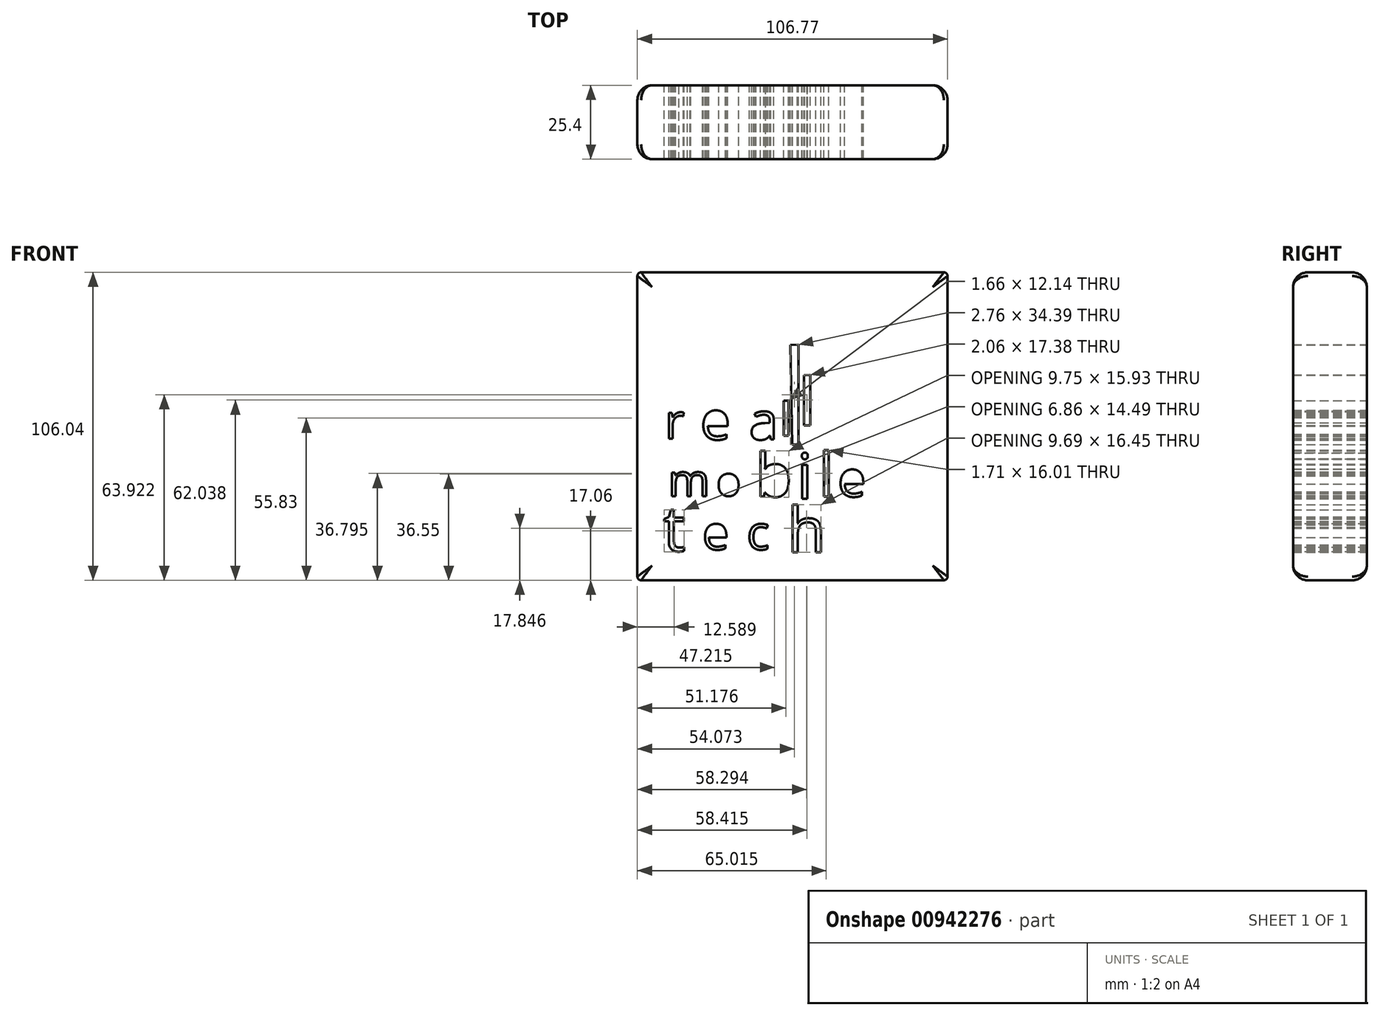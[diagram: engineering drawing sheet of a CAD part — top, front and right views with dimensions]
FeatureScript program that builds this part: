
annotation { "Feature Type Name" : "Feature", "Feature Type Description" : "" }
export const myFeature = defineFeature(function(context is Context, id is Id, definition is map)
    precondition{}
    {
        {
            var Q0;
            Q0=qCreatedBy(makeId("Front.planeOp"),FACE);
            var sketch = newSketch(context, id + "F0", { "sketchPlane" : qUnion([Q0])});
            skText(sketch, "E0", { "text": "r", "fontName": "OpenSans-Regular.ttf"});
            skText(sketch, "E1", { "text": "e", "fontName": "OpenSans-Regular.ttf"});
            skText(sketch, "E2", { "text": "a\n", "fontName": "OpenSans-Regular.ttf"});
            skLineSegment(sketch, "E3", {"start": v(-13.31, 13.45) * mm, "end": v(-13.31, 1.31) * mm});
            skLineSegment(sketch, "E4", {"start": v(-13.31, 1.31) * mm, "end": v(-11.66, 1.31) * mm});
            skLineSegment(sketch, "E5", {"start": v(-11.66, 1.31) * mm, "end": v(-11.66, 13.45) * mm});
            skLineSegment(sketch, "E6", {"start": v(-11.66, 13.45) * mm, "end": v(-13.31, 13.45) * mm});
            skLineSegment(sketch, "E7", {"start": v(-10.42, -1.72) * mm, "end": v(-8.2, -1.72) * mm});
            skLineSegment(sketch, "E8", {"start": v(-10.97, 32.62) * mm, "end": v(-10.42, -1.72) * mm});
            skLineSegment(sketch, "E9", {"start": v(-10.97, 32.62) * mm, "end": v(-8.2, 32.67) * mm});
            skLineSegment(sketch, "E10", {"start": v(-8.2, 32.67) * mm, "end": v(-8.2, -1.72) * mm});
            skLineSegment(sketch, "E11", {"start": v(-6.28, 22.14) * mm, "end": v(-6.28, 4.9) * mm});
            skLineSegment(sketch, "E12", {"start": v(-6.28, 4.9) * mm, "end": v(-4.21, 4.93) * mm});
            skLineSegment(sketch, "E13", {"start": v(-4.21, 4.93) * mm, "end": v(-4.21, 22.28) * mm});
            skLineSegment(sketch, "E14", {"start": v(-4.21, 22.28) * mm, "end": v(-6.28, 22.14) * mm});
            skText(sketch, "E15", { "text": "m", "fontName": "OpenSans-Regular.ttf"});
            skText(sketch, "E16", { "text": "o", "fontName": "OpenSans-Regular.ttf"});
            skText(sketch, "E17", { "text": "b", "fontName": "OpenSans-Regular.ttf"});
            skText(sketch, "E18", { "text": "i", "fontName": "OpenSans-Regular.ttf"});
            skText(sketch, "E19", { "text": "l", "fontName": "OpenSans-Regular.ttf"});
            skText(sketch, "E20", { "text": "e", "fontName": "OpenSans-Regular.ttf"});
            skText(sketch, "E21", { "text": "t\n", "fontName": "OpenSans-Regular.ttf"});
            skText(sketch, "E22", { "text": "e", "fontName": "OpenSans-Regular.ttf"});
            skText(sketch, "E23", { "text": "c", "fontName": "OpenSans-Regular.ttf"});
            skText(sketch, "E24", { "text": "h", "fontName": "OpenSans-Regular.ttf"});
            skLineSegment(sketch, "E25", {"start": v(-63.66, 57.6) * mm, "end": v(-63.66, -50.42) * mm});
            skLineSegment(sketch, "E26", {"start": v(-63.66, -48.45) * mm, "end": v(43.1, -48.45) * mm});
            skLineSegment(sketch, "E27", {"start": v(43.1, 57.6) * mm, "end": v(43.1, -48.45) * mm});
            skLineSegment(sketch, "E28", {"start": v(-63.66, 57.6) * mm, "end": v(43.1, 57.6) * mm});
            const initialGuessF0  = {"E0": [-0.05428, 0.00034, 1, 0, 0.012], "E1": [-0.042, 0, 1, 0, 0.01331], "E2": [-0.02518, 0, 1, 0, 0.0129], "E15": [-0.05304, -0.01952, 1, 0, 0.01104], "E16": [-0.03649, -0.01938, 1, 0, 0.01007], "E17": [-0.0231, -0.01966, 1, 0, 0.0149], "E18": [-0.00876, -0.02035, 1, 0, 0.01559], "E19": [-0.00131, -0.01966, 1, 0, 0.01517], "E20": [0.00531, -0.01966, 1, 0, 0.01242], "E21": [-0.05483, -0.03842, 1, 0, 0.01559], "E22": [-0.04132, -0.03787, 1, 0, 0.01173], "E23": [-0.026, -0.03787, 1, 0, 0.01173], "E24": [-0.01207, -0.03883, 1, 0, 0.01559]};
            skSetInitialGuess(sketch, initialGuessF0);
            skSolve(sketch);
        }
        {
            var Q0;
            Q0 = qSketchRegion(id + "F0", true);
            extrude(context, id + "F1", {"entities" : qUnion([Q0]), "depth" : 25.4 * mm, "offsetDistance" : 25.4 * mm});
        }
        {
            var Q0;
            Q0=makeQuery(id+"F1.opExtrude","SWEPT_EDGE",EDGE,{"disambiguationData":[OSD([sQuery(id+"F0.wireOp",EDGE,"E27"),sQuery(id+"F0.wireOp",EDGE,"E28")])]});
            var Q1;
            Q1=makeQuery(id+"F1.opExtrude","SWEPT_EDGE",EDGE,{"disambiguationData":[OSD([sQuery(id+"F0.wireOp",EDGE,"E26"),sQuery(id+"F0.wireOp",EDGE,"E27")])]});
            var Q2;
            Q2=makeQuery(id+"F1.opExtrude","SWEPT_EDGE",EDGE,{"disambiguationData":[OSD([sQuery(id+"F0.wireOp",EDGE,"E25"),sQuery(id+"F0.wireOp",EDGE,"E26")])]});
            var Q3;
            Q3=makeQuery(id+"F1.opExtrude","SWEPT_EDGE",EDGE,{"disambiguationData":[OSD([sQuery(id+"F0.wireOp",EDGE,"E25"),sQuery(id+"F0.wireOp",EDGE,"E28")])]});
            fillet(context, id + "F2", {"entities" : qUnion([Q0, Q1, Q2, Q3]), "radius" : 1.27 * mm, "tangentPropagation" : true, "allowEdgeOverflow" : false});
        }
        {
            var Q0;
            Q0=makeQuery(id+"F1.opExtrude","CAP_EDGE",EDGE,{"disambiguationData":[OSD([sQuery(id+"F0.wireOp",EDGE,"E28")])],"isStart":false});
            var Q1;
            {var subQ0=sQuery(id+"F0.wireOp",EDGE,"E28");var subQ1=sQuery(id+"F0.wireOp",EDGE,"E27");Q1=makeQuery(id+"F2.opFillet","BLEND_EDGE",EDGE,{"blendedFrom":[makeQuery(id+"F1.opExtrude","SWEPT_EDGE",EDGE,{"disambiguationData":[OSD([subQ1,subQ0])]}),makeQuery(id+"F1.opExtrude","CAP_FACE",FACE,{"disambiguationData":[OSD([sQuery(id+"F0.wireOp",EDGE,"E0.sketch_text.stroke-0"),sQuery(id+"F0.wireOp",EDGE,"E0.sketch_text.stroke-1"),sQuery(id+"F0.wireOp",EDGE,"E0.sketch_text.stroke-2"),sQuery(id+"F0.wireOp",EDGE,"E0.sketch_text.stroke-3"),sQuery(id+"F0.wireOp",EDGE,"E0.sketch_text.stroke-4"),sQuery(id+"F0.wireOp",EDGE,"E0.sketch_text.stroke-5"),sQuery(id+"F0.wireOp",EDGE,"E0.sketch_text.stroke-6"),sQuery(id+"F0.wireOp",EDGE,"E0.sketch_text.stroke-7"),sQuery(id+"F0.wireOp",EDGE,"E0.sketch_text.stroke-8"),sQuery(id+"F0.wireOp",EDGE,"E0.sketch_text.stroke-9"),sQuery(id+"F0.wireOp",EDGE,"E0.sketch_text.stroke-10"),sQuery(id+"F0.wireOp",EDGE,"E0.sketch_text.stroke-11"),sQuery(id+"F0.wireOp",EDGE,"E0.sketch_text.stroke-12"),sQuery(id+"F0.wireOp",EDGE,"E1.sketch_text.stroke-0"),sQuery(id+"F0.wireOp",EDGE,"E1.sketch_text.stroke-1"),sQuery(id+"F0.wireOp",EDGE,"E1.sketch_text.stroke-2"),sQuery(id+"F0.wireOp",EDGE,"E1.sketch_text.stroke-3"),sQuery(id+"F0.wireOp",EDGE,"E1.sketch_text.stroke-4"),sQuery(id+"F0.wireOp",EDGE,"E1.sketch_text.stroke-5"),sQuery(id+"F0.wireOp",EDGE,"E1.sketch_text.stroke-6"),sQuery(id+"F0.wireOp",EDGE,"E1.sketch_text.stroke-7"),sQuery(id+"F0.wireOp",EDGE,"E1.sketch_text.stroke-8"),sQuery(id+"F0.wireOp",EDGE,"E1.sketch_text.stroke-9"),sQuery(id+"F0.wireOp",EDGE,"E1.sketch_text.stroke-10"),sQuery(id+"F0.wireOp",EDGE,"E1.sketch_text.stroke-11"),sQuery(id+"F0.wireOp",EDGE,"E1.sketch_text.stroke-12"),sQuery(id+"F0.wireOp",EDGE,"E1.sketch_text.stroke-13"),sQuery(id+"F0.wireOp",EDGE,"E2.sketch_text.stroke-0"),sQuery(id+"F0.wireOp",EDGE,"E2.sketch_text.stroke-1"),sQuery(id+"F0.wireOp",EDGE,"E2.sketch_text.stroke-2"),sQuery(id+"F0.wireOp",EDGE,"E2.sketch_text.stroke-3"),sQuery(id+"F0.wireOp",EDGE,"E2.sketch_text.stroke-4"),sQuery(id+"F0.wireOp",EDGE,"E2.sketch_text.stroke-5"),sQuery(id+"F0.wireOp",EDGE,"E2.sketch_text.stroke-6"),sQuery(id+"F0.wireOp",EDGE,"E2.sketch_text.stroke-7"),sQuery(id+"F0.wireOp",EDGE,"E2.sketch_text.stroke-8"),sQuery(id+"F0.wireOp",EDGE,"E2.sketch_text.stroke-9"),sQuery(id+"F0.wireOp",EDGE,"E2.sketch_text.stroke-10"),sQuery(id+"F0.wireOp",EDGE,"E2.sketch_text.stroke-11"),sQuery(id+"F0.wireOp",EDGE,"E2.sketch_text.stroke-12"),sQuery(id+"F0.wireOp",EDGE,"E2.sketch_text.stroke-13"),sQuery(id+"F0.wireOp",EDGE,"E2.sketch_text.stroke-14"),sQuery(id+"F0.wireOp",EDGE,"E2.sketch_text.stroke-15"),sQuery(id+"F0.wireOp",EDGE,"E2.sketch_text.stroke-16"),sQuery(id+"F0.wireOp",EDGE,"E2.sketch_text.stroke-17"),sQuery(id+"F0.wireOp",EDGE,"E2.sketch_text.stroke-18"),sQuery(id+"F0.wireOp",EDGE,"E3"),sQuery(id+"F0.wireOp",EDGE,"E4"),sQuery(id+"F0.wireOp",EDGE,"E5"),sQuery(id+"F0.wireOp",EDGE,"E6"),sQuery(id+"F0.wireOp",EDGE,"E7"),sQuery(id+"F0.wireOp",EDGE,"E8"),sQuery(id+"F0.wireOp",EDGE,"E9"),sQuery(id+"F0.wireOp",EDGE,"E10"),sQuery(id+"F0.wireOp",EDGE,"E11"),sQuery(id+"F0.wireOp",EDGE,"E12"),sQuery(id+"F0.wireOp",EDGE,"E13"),sQuery(id+"F0.wireOp",EDGE,"E14"),sQuery(id+"F0.wireOp",EDGE,"E15.sketch_text.stroke-0"),sQuery(id+"F0.wireOp",EDGE,"E15.sketch_text.stroke-1"),sQuery(id+"F0.wireOp",EDGE,"E15.sketch_text.stroke-2"),sQuery(id+"F0.wireOp",EDGE,"E15.sketch_text.stroke-3"),sQuery(id+"F0.wireOp",EDGE,"E15.sketch_text.stroke-4"),sQuery(id+"F0.wireOp",EDGE,"E15.sketch_text.stroke-5"),sQuery(id+"F0.wireOp",EDGE,"E15.sketch_text.stroke-6"),sQuery(id+"F0.wireOp",EDGE,"E15.sketch_text.stroke-7"),sQuery(id+"F0.wireOp",EDGE,"E15.sketch_text.stroke-8"),sQuery(id+"F0.wireOp",EDGE,"E15.sketch_text.stroke-9"),sQuery(id+"F0.wireOp",EDGE,"E15.sketch_text.stroke-10"),sQuery(id+"F0.wireOp",EDGE,"E15.sketch_text.stroke-11"),sQuery(id+"F0.wireOp",EDGE,"E15.sketch_text.stroke-12"),sQuery(id+"F0.wireOp",EDGE,"E15.sketch_text.stroke-13"),sQuery(id+"F0.wireOp",EDGE,"E15.sketch_text.stroke-14"),sQuery(id+"F0.wireOp",EDGE,"E15.sketch_text.stroke-15"),sQuery(id+"F0.wireOp",EDGE,"E15.sketch_text.stroke-16"),sQuery(id+"F0.wireOp",EDGE,"E15.sketch_text.stroke-17"),sQuery(id+"F0.wireOp",EDGE,"E15.sketch_text.stroke-18"),sQuery(id+"F0.wireOp",EDGE,"E15.sketch_text.stroke-19"),sQuery(id+"F0.wireOp",EDGE,"E15.sketch_text.stroke-20"),sQuery(id+"F0.wireOp",EDGE,"E15.sketch_text.stroke-21"),sQuery(id+"F0.wireOp",EDGE,"E15.sketch_text.stroke-22"),sQuery(id+"F0.wireOp",EDGE,"E15.sketch_text.stroke-23"),sQuery(id+"F0.wireOp",EDGE,"E15.sketch_text.stroke-24"),sQuery(id+"F0.wireOp",EDGE,"E15.sketch_text.stroke-25"),sQuery(id+"F0.wireOp",EDGE,"E15.sketch_text.stroke-26"),sQuery(id+"F0.wireOp",EDGE,"E15.sketch_text.stroke-27"),sQuery(id+"F0.wireOp",EDGE,"E16.sketch_text.stroke-0"),sQuery(id+"F0.wireOp",EDGE,"E16.sketch_text.stroke-1"),sQuery(id+"F0.wireOp",EDGE,"E16.sketch_text.stroke-2"),sQuery(id+"F0.wireOp",EDGE,"E16.sketch_text.stroke-3"),sQuery(id+"F0.wireOp",EDGE,"E16.sketch_text.stroke-4"),sQuery(id+"F0.wireOp",EDGE,"E16.sketch_text.stroke-5"),sQuery(id+"F0.wireOp",EDGE,"E16.sketch_text.stroke-6"),sQuery(id+"F0.wireOp",EDGE,"E16.sketch_text.stroke-7"),sQuery(id+"F0.wireOp",EDGE,"E16.sketch_text.stroke-8"),sQuery(id+"F0.wireOp",EDGE,"E17.sketch_text.stroke-0"),sQuery(id+"F0.wireOp",EDGE,"E17.sketch_text.stroke-1"),sQuery(id+"F0.wireOp",EDGE,"E17.sketch_text.stroke-2"),sQuery(id+"F0.wireOp",EDGE,"E17.sketch_text.stroke-3"),sQuery(id+"F0.wireOp",EDGE,"E17.sketch_text.stroke-4"),sQuery(id+"F0.wireOp",EDGE,"E17.sketch_text.stroke-5"),sQuery(id+"F0.wireOp",EDGE,"E17.sketch_text.stroke-6"),sQuery(id+"F0.wireOp",EDGE,"E17.sketch_text.stroke-7"),sQuery(id+"F0.wireOp",EDGE,"E17.sketch_text.stroke-8"),sQuery(id+"F0.wireOp",EDGE,"E17.sketch_text.stroke-9"),sQuery(id+"F0.wireOp",EDGE,"E17.sketch_text.stroke-10"),sQuery(id+"F0.wireOp",EDGE,"E17.sketch_text.stroke-11"),sQuery(id+"F0.wireOp",EDGE,"E17.sketch_text.stroke-12"),sQuery(id+"F0.wireOp",EDGE,"E17.sketch_text.stroke-13"),sQuery(id+"F0.wireOp",EDGE,"E17.sketch_text.stroke-14"),sQuery(id+"F0.wireOp",EDGE,"E18.sketch_text.stroke-0"),sQuery(id+"F0.wireOp",EDGE,"E18.sketch_text.stroke-1"),sQuery(id+"F0.wireOp",EDGE,"E18.sketch_text.stroke-2"),sQuery(id+"F0.wireOp",EDGE,"E18.sketch_text.stroke-3"),sQuery(id+"F0.wireOp",EDGE,"E18.sketch_text.stroke-4"),sQuery(id+"F0.wireOp",EDGE,"E18.sketch_text.stroke-5"),sQuery(id+"F0.wireOp",EDGE,"E18.sketch_text.stroke-6"),sQuery(id+"F0.wireOp",EDGE,"E18.sketch_text.stroke-7"),sQuery(id+"F0.wireOp",EDGE,"E18.sketch_text.stroke-8"),sQuery(id+"F0.wireOp",EDGE,"E18.sketch_text.stroke-9"),sQuery(id+"F0.wireOp",EDGE,"E18.sketch_text.stroke-10"),sQuery(id+"F0.wireOp",EDGE,"E18.sketch_text.stroke-11"),sQuery(id+"F0.wireOp",EDGE,"E19.sketch_text.stroke-0"),sQuery(id+"F0.wireOp",EDGE,"E19.sketch_text.stroke-1"),sQuery(id+"F0.wireOp",EDGE,"E19.sketch_text.stroke-2"),sQuery(id+"F0.wireOp",EDGE,"E19.sketch_text.stroke-3"),sQuery(id+"F0.wireOp",EDGE,"E20.sketch_text.stroke-0"),sQuery(id+"F0.wireOp",EDGE,"E20.sketch_text.stroke-1"),sQuery(id+"F0.wireOp",EDGE,"E20.sketch_text.stroke-2"),sQuery(id+"F0.wireOp",EDGE,"E20.sketch_text.stroke-3"),sQuery(id+"F0.wireOp",EDGE,"E20.sketch_text.stroke-4"),sQuery(id+"F0.wireOp",EDGE,"E20.sketch_text.stroke-5"),sQuery(id+"F0.wireOp",EDGE,"E20.sketch_text.stroke-6"),sQuery(id+"F0.wireOp",EDGE,"E20.sketch_text.stroke-7"),sQuery(id+"F0.wireOp",EDGE,"E20.sketch_text.stroke-8"),sQuery(id+"F0.wireOp",EDGE,"E20.sketch_text.stroke-9"),sQuery(id+"F0.wireOp",EDGE,"E20.sketch_text.stroke-10"),sQuery(id+"F0.wireOp",EDGE,"E20.sketch_text.stroke-11"),sQuery(id+"F0.wireOp",EDGE,"E20.sketch_text.stroke-12"),sQuery(id+"F0.wireOp",EDGE,"E20.sketch_text.stroke-13"),sQuery(id+"F0.wireOp",EDGE,"E21.sketch_text.stroke-0"),sQuery(id+"F0.wireOp",EDGE,"E21.sketch_text.stroke-1"),sQuery(id+"F0.wireOp",EDGE,"E21.sketch_text.stroke-2"),sQuery(id+"F0.wireOp",EDGE,"E21.sketch_text.stroke-3"),sQuery(id+"F0.wireOp",EDGE,"E21.sketch_text.stroke-4"),sQuery(id+"F0.wireOp",EDGE,"E21.sketch_text.stroke-5"),sQuery(id+"F0.wireOp",EDGE,"E21.sketch_text.stroke-6"),sQuery(id+"F0.wireOp",EDGE,"E21.sketch_text.stroke-7"),sQuery(id+"F0.wireOp",EDGE,"E21.sketch_text.stroke-8"),sQuery(id+"F0.wireOp",EDGE,"E21.sketch_text.stroke-9"),sQuery(id+"F0.wireOp",EDGE,"E21.sketch_text.stroke-10"),sQuery(id+"F0.wireOp",EDGE,"E21.sketch_text.stroke-11"),sQuery(id+"F0.wireOp",EDGE,"E21.sketch_text.stroke-12"),sQuery(id+"F0.wireOp",EDGE,"E21.sketch_text.stroke-13"),sQuery(id+"F0.wireOp",EDGE,"E21.sketch_text.stroke-14"),sQuery(id+"F0.wireOp",EDGE,"E21.sketch_text.stroke-15"),sQuery(id+"F0.wireOp",EDGE,"E21.sketch_text.stroke-16"),sQuery(id+"F0.wireOp",EDGE,"E21.sketch_text.stroke-17"),sQuery(id+"F0.wireOp",EDGE,"E21.sketch_text.stroke-18"),sQuery(id+"F0.wireOp",EDGE,"E22.sketch_text.stroke-0"),sQuery(id+"F0.wireOp",EDGE,"E22.sketch_text.stroke-1"),sQuery(id+"F0.wireOp",EDGE,"E22.sketch_text.stroke-2"),sQuery(id+"F0.wireOp",EDGE,"E22.sketch_text.stroke-3"),sQuery(id+"F0.wireOp",EDGE,"E22.sketch_text.stroke-4"),sQuery(id+"F0.wireOp",EDGE,"E22.sketch_text.stroke-5"),sQuery(id+"F0.wireOp",EDGE,"E22.sketch_text.stroke-6"),sQuery(id+"F0.wireOp",EDGE,"E22.sketch_text.stroke-7"),sQuery(id+"F0.wireOp",EDGE,"E22.sketch_text.stroke-8"),sQuery(id+"F0.wireOp",EDGE,"E22.sketch_text.stroke-9"),sQuery(id+"F0.wireOp",EDGE,"E22.sketch_text.stroke-10"),sQuery(id+"F0.wireOp",EDGE,"E22.sketch_text.stroke-11"),sQuery(id+"F0.wireOp",EDGE,"E22.sketch_text.stroke-12"),sQuery(id+"F0.wireOp",EDGE,"E22.sketch_text.stroke-13"),sQuery(id+"F0.wireOp",EDGE,"E23.sketch_text.stroke-0"),sQuery(id+"F0.wireOp",EDGE,"E23.sketch_text.stroke-1"),sQuery(id+"F0.wireOp",EDGE,"E23.sketch_text.stroke-2"),sQuery(id+"F0.wireOp",EDGE,"E23.sketch_text.stroke-3"),sQuery(id+"F0.wireOp",EDGE,"E23.sketch_text.stroke-4"),sQuery(id+"F0.wireOp",EDGE,"E23.sketch_text.stroke-5"),sQuery(id+"F0.wireOp",EDGE,"E23.sketch_text.stroke-6"),sQuery(id+"F0.wireOp",EDGE,"E23.sketch_text.stroke-7"),sQuery(id+"F0.wireOp",EDGE,"E23.sketch_text.stroke-8"),sQuery(id+"F0.wireOp",EDGE,"E23.sketch_text.stroke-9"),sQuery(id+"F0.wireOp",EDGE,"E23.sketch_text.stroke-10"),sQuery(id+"F0.wireOp",EDGE,"E23.sketch_text.stroke-11"),sQuery(id+"F0.wireOp",EDGE,"E23.sketch_text.stroke-12"),sQuery(id+"F0.wireOp",EDGE,"E23.sketch_text.stroke-13"),sQuery(id+"F0.wireOp",EDGE,"E23.sketch_text.stroke-14"),sQuery(id+"F0.wireOp",EDGE,"E24.sketch_text.stroke-0"),sQuery(id+"F0.wireOp",EDGE,"E24.sketch_text.stroke-1"),sQuery(id+"F0.wireOp",EDGE,"E24.sketch_text.stroke-2"),sQuery(id+"F0.wireOp",EDGE,"E24.sketch_text.stroke-3"),sQuery(id+"F0.wireOp",EDGE,"E24.sketch_text.stroke-4"),sQuery(id+"F0.wireOp",EDGE,"E24.sketch_text.stroke-5"),sQuery(id+"F0.wireOp",EDGE,"E24.sketch_text.stroke-6"),sQuery(id+"F0.wireOp",EDGE,"E24.sketch_text.stroke-7"),sQuery(id+"F0.wireOp",EDGE,"E24.sketch_text.stroke-8"),sQuery(id+"F0.wireOp",EDGE,"E24.sketch_text.stroke-9"),sQuery(id+"F0.wireOp",EDGE,"E24.sketch_text.stroke-10"),sQuery(id+"F0.wireOp",EDGE,"E24.sketch_text.stroke-11"),sQuery(id+"F0.wireOp",EDGE,"E24.sketch_text.stroke-12"),sQuery(id+"F0.wireOp",EDGE,"E24.sketch_text.stroke-13"),sQuery(id+"F0.wireOp",EDGE,"E24.sketch_text.stroke-14"),sQuery(id+"F0.wireOp",EDGE,"E24.sketch_text.stroke-15"),sQuery(id+"F0.wireOp",EDGE,"E24.sketch_text.stroke-16"),sQuery(id+"F0.wireOp",EDGE,"E24.sketch_text.stroke-17"),sQuery(id+"F0.wireOp",EDGE,"E25"),sQuery(id+"F0.wireOp",EDGE,"E26"),subQ1,subQ0])],"isStart":false})],"blendedInto":[makeQuery(id+"F1.opExtrude","CAP_FACE",FACE,{"disambiguationData":[OSD([sQuery(id+"F0.wireOp",EDGE,"E0.sketch_text.stroke-0"),sQuery(id+"F0.wireOp",EDGE,"E0.sketch_text.stroke-1"),sQuery(id+"F0.wireOp",EDGE,"E0.sketch_text.stroke-2"),sQuery(id+"F0.wireOp",EDGE,"E0.sketch_text.stroke-3"),sQuery(id+"F0.wireOp",EDGE,"E0.sketch_text.stroke-4"),sQuery(id+"F0.wireOp",EDGE,"E0.sketch_text.stroke-5"),sQuery(id+"F0.wireOp",EDGE,"E0.sketch_text.stroke-6"),sQuery(id+"F0.wireOp",EDGE,"E0.sketch_text.stroke-7"),sQuery(id+"F0.wireOp",EDGE,"E0.sketch_text.stroke-8"),sQuery(id+"F0.wireOp",EDGE,"E0.sketch_text.stroke-9"),sQuery(id+"F0.wireOp",EDGE,"E0.sketch_text.stroke-10"),sQuery(id+"F0.wireOp",EDGE,"E0.sketch_text.stroke-11"),sQuery(id+"F0.wireOp",EDGE,"E0.sketch_text.stroke-12"),sQuery(id+"F0.wireOp",EDGE,"E1.sketch_text.stroke-0"),sQuery(id+"F0.wireOp",EDGE,"E1.sketch_text.stroke-1"),sQuery(id+"F0.wireOp",EDGE,"E1.sketch_text.stroke-2"),sQuery(id+"F0.wireOp",EDGE,"E1.sketch_text.stroke-3"),sQuery(id+"F0.wireOp",EDGE,"E1.sketch_text.stroke-4"),sQuery(id+"F0.wireOp",EDGE,"E1.sketch_text.stroke-5"),sQuery(id+"F0.wireOp",EDGE,"E1.sketch_text.stroke-6"),sQuery(id+"F0.wireOp",EDGE,"E1.sketch_text.stroke-7"),sQuery(id+"F0.wireOp",EDGE,"E1.sketch_text.stroke-8"),sQuery(id+"F0.wireOp",EDGE,"E1.sketch_text.stroke-9"),sQuery(id+"F0.wireOp",EDGE,"E1.sketch_text.stroke-10"),sQuery(id+"F0.wireOp",EDGE,"E1.sketch_text.stroke-11"),sQuery(id+"F0.wireOp",EDGE,"E1.sketch_text.stroke-12"),sQuery(id+"F0.wireOp",EDGE,"E1.sketch_text.stroke-13"),sQuery(id+"F0.wireOp",EDGE,"E2.sketch_text.stroke-0"),sQuery(id+"F0.wireOp",EDGE,"E2.sketch_text.stroke-1"),sQuery(id+"F0.wireOp",EDGE,"E2.sketch_text.stroke-2"),sQuery(id+"F0.wireOp",EDGE,"E2.sketch_text.stroke-3"),sQuery(id+"F0.wireOp",EDGE,"E2.sketch_text.stroke-4"),sQuery(id+"F0.wireOp",EDGE,"E2.sketch_text.stroke-5"),sQuery(id+"F0.wireOp",EDGE,"E2.sketch_text.stroke-6"),sQuery(id+"F0.wireOp",EDGE,"E2.sketch_text.stroke-7"),sQuery(id+"F0.wireOp",EDGE,"E2.sketch_text.stroke-8"),sQuery(id+"F0.wireOp",EDGE,"E2.sketch_text.stroke-9"),sQuery(id+"F0.wireOp",EDGE,"E2.sketch_text.stroke-10"),sQuery(id+"F0.wireOp",EDGE,"E2.sketch_text.stroke-11"),sQuery(id+"F0.wireOp",EDGE,"E2.sketch_text.stroke-12"),sQuery(id+"F0.wireOp",EDGE,"E2.sketch_text.stroke-13"),sQuery(id+"F0.wireOp",EDGE,"E2.sketch_text.stroke-14"),sQuery(id+"F0.wireOp",EDGE,"E2.sketch_text.stroke-15"),sQuery(id+"F0.wireOp",EDGE,"E2.sketch_text.stroke-16"),sQuery(id+"F0.wireOp",EDGE,"E2.sketch_text.stroke-17"),sQuery(id+"F0.wireOp",EDGE,"E2.sketch_text.stroke-18"),sQuery(id+"F0.wireOp",EDGE,"E3"),sQuery(id+"F0.wireOp",EDGE,"E4"),sQuery(id+"F0.wireOp",EDGE,"E5"),sQuery(id+"F0.wireOp",EDGE,"E6"),sQuery(id+"F0.wireOp",EDGE,"E7"),sQuery(id+"F0.wireOp",EDGE,"E8"),sQuery(id+"F0.wireOp",EDGE,"E9"),sQuery(id+"F0.wireOp",EDGE,"E10"),sQuery(id+"F0.wireOp",EDGE,"E11"),sQuery(id+"F0.wireOp",EDGE,"E12"),sQuery(id+"F0.wireOp",EDGE,"E13"),sQuery(id+"F0.wireOp",EDGE,"E14"),sQuery(id+"F0.wireOp",EDGE,"E15.sketch_text.stroke-0"),sQuery(id+"F0.wireOp",EDGE,"E15.sketch_text.stroke-1"),sQuery(id+"F0.wireOp",EDGE,"E15.sketch_text.stroke-2"),sQuery(id+"F0.wireOp",EDGE,"E15.sketch_text.stroke-3"),sQuery(id+"F0.wireOp",EDGE,"E15.sketch_text.stroke-4"),sQuery(id+"F0.wireOp",EDGE,"E15.sketch_text.stroke-5"),sQuery(id+"F0.wireOp",EDGE,"E15.sketch_text.stroke-6"),sQuery(id+"F0.wireOp",EDGE,"E15.sketch_text.stroke-7"),sQuery(id+"F0.wireOp",EDGE,"E15.sketch_text.stroke-8"),sQuery(id+"F0.wireOp",EDGE,"E15.sketch_text.stroke-9"),sQuery(id+"F0.wireOp",EDGE,"E15.sketch_text.stroke-10"),sQuery(id+"F0.wireOp",EDGE,"E15.sketch_text.stroke-11"),sQuery(id+"F0.wireOp",EDGE,"E15.sketch_text.stroke-12"),sQuery(id+"F0.wireOp",EDGE,"E15.sketch_text.stroke-13"),sQuery(id+"F0.wireOp",EDGE,"E15.sketch_text.stroke-14"),sQuery(id+"F0.wireOp",EDGE,"E15.sketch_text.stroke-15"),sQuery(id+"F0.wireOp",EDGE,"E15.sketch_text.stroke-16"),sQuery(id+"F0.wireOp",EDGE,"E15.sketch_text.stroke-17"),sQuery(id+"F0.wireOp",EDGE,"E15.sketch_text.stroke-18"),sQuery(id+"F0.wireOp",EDGE,"E15.sketch_text.stroke-19"),sQuery(id+"F0.wireOp",EDGE,"E15.sketch_text.stroke-20"),sQuery(id+"F0.wireOp",EDGE,"E15.sketch_text.stroke-21"),sQuery(id+"F0.wireOp",EDGE,"E15.sketch_text.stroke-22"),sQuery(id+"F0.wireOp",EDGE,"E15.sketch_text.stroke-23"),sQuery(id+"F0.wireOp",EDGE,"E15.sketch_text.stroke-24"),sQuery(id+"F0.wireOp",EDGE,"E15.sketch_text.stroke-25"),sQuery(id+"F0.wireOp",EDGE,"E15.sketch_text.stroke-26"),sQuery(id+"F0.wireOp",EDGE,"E15.sketch_text.stroke-27"),sQuery(id+"F0.wireOp",EDGE,"E16.sketch_text.stroke-0"),sQuery(id+"F0.wireOp",EDGE,"E16.sketch_text.stroke-1"),sQuery(id+"F0.wireOp",EDGE,"E16.sketch_text.stroke-2"),sQuery(id+"F0.wireOp",EDGE,"E16.sketch_text.stroke-3"),sQuery(id+"F0.wireOp",EDGE,"E16.sketch_text.stroke-4"),sQuery(id+"F0.wireOp",EDGE,"E16.sketch_text.stroke-5"),sQuery(id+"F0.wireOp",EDGE,"E16.sketch_text.stroke-6"),sQuery(id+"F0.wireOp",EDGE,"E16.sketch_text.stroke-7"),sQuery(id+"F0.wireOp",EDGE,"E16.sketch_text.stroke-8"),sQuery(id+"F0.wireOp",EDGE,"E17.sketch_text.stroke-0"),sQuery(id+"F0.wireOp",EDGE,"E17.sketch_text.stroke-1"),sQuery(id+"F0.wireOp",EDGE,"E17.sketch_text.stroke-2"),sQuery(id+"F0.wireOp",EDGE,"E17.sketch_text.stroke-3"),sQuery(id+"F0.wireOp",EDGE,"E17.sketch_text.stroke-4"),sQuery(id+"F0.wireOp",EDGE,"E17.sketch_text.stroke-5"),sQuery(id+"F0.wireOp",EDGE,"E17.sketch_text.stroke-6"),sQuery(id+"F0.wireOp",EDGE,"E17.sketch_text.stroke-7"),sQuery(id+"F0.wireOp",EDGE,"E17.sketch_text.stroke-8"),sQuery(id+"F0.wireOp",EDGE,"E17.sketch_text.stroke-9"),sQuery(id+"F0.wireOp",EDGE,"E17.sketch_text.stroke-10"),sQuery(id+"F0.wireOp",EDGE,"E17.sketch_text.stroke-11"),sQuery(id+"F0.wireOp",EDGE,"E17.sketch_text.stroke-12"),sQuery(id+"F0.wireOp",EDGE,"E17.sketch_text.stroke-13"),sQuery(id+"F0.wireOp",EDGE,"E17.sketch_text.stroke-14"),sQuery(id+"F0.wireOp",EDGE,"E18.sketch_text.stroke-0"),sQuery(id+"F0.wireOp",EDGE,"E18.sketch_text.stroke-1"),sQuery(id+"F0.wireOp",EDGE,"E18.sketch_text.stroke-2"),sQuery(id+"F0.wireOp",EDGE,"E18.sketch_text.stroke-3"),sQuery(id+"F0.wireOp",EDGE,"E18.sketch_text.stroke-4"),sQuery(id+"F0.wireOp",EDGE,"E18.sketch_text.stroke-5"),sQuery(id+"F0.wireOp",EDGE,"E18.sketch_text.stroke-6"),sQuery(id+"F0.wireOp",EDGE,"E18.sketch_text.stroke-7"),sQuery(id+"F0.wireOp",EDGE,"E18.sketch_text.stroke-8"),sQuery(id+"F0.wireOp",EDGE,"E18.sketch_text.stroke-9"),sQuery(id+"F0.wireOp",EDGE,"E18.sketch_text.stroke-10"),sQuery(id+"F0.wireOp",EDGE,"E18.sketch_text.stroke-11"),sQuery(id+"F0.wireOp",EDGE,"E19.sketch_text.stroke-0"),sQuery(id+"F0.wireOp",EDGE,"E19.sketch_text.stroke-1"),sQuery(id+"F0.wireOp",EDGE,"E19.sketch_text.stroke-2"),sQuery(id+"F0.wireOp",EDGE,"E19.sketch_text.stroke-3"),sQuery(id+"F0.wireOp",EDGE,"E20.sketch_text.stroke-0"),sQuery(id+"F0.wireOp",EDGE,"E20.sketch_text.stroke-1"),sQuery(id+"F0.wireOp",EDGE,"E20.sketch_text.stroke-2"),sQuery(id+"F0.wireOp",EDGE,"E20.sketch_text.stroke-3"),sQuery(id+"F0.wireOp",EDGE,"E20.sketch_text.stroke-4"),sQuery(id+"F0.wireOp",EDGE,"E20.sketch_text.stroke-5"),sQuery(id+"F0.wireOp",EDGE,"E20.sketch_text.stroke-6"),sQuery(id+"F0.wireOp",EDGE,"E20.sketch_text.stroke-7"),sQuery(id+"F0.wireOp",EDGE,"E20.sketch_text.stroke-8"),sQuery(id+"F0.wireOp",EDGE,"E20.sketch_text.stroke-9"),sQuery(id+"F0.wireOp",EDGE,"E20.sketch_text.stroke-10"),sQuery(id+"F0.wireOp",EDGE,"E20.sketch_text.stroke-11"),sQuery(id+"F0.wireOp",EDGE,"E20.sketch_text.stroke-12"),sQuery(id+"F0.wireOp",EDGE,"E20.sketch_text.stroke-13"),sQuery(id+"F0.wireOp",EDGE,"E21.sketch_text.stroke-0"),sQuery(id+"F0.wireOp",EDGE,"E21.sketch_text.stroke-1"),sQuery(id+"F0.wireOp",EDGE,"E21.sketch_text.stroke-2"),sQuery(id+"F0.wireOp",EDGE,"E21.sketch_text.stroke-3"),sQuery(id+"F0.wireOp",EDGE,"E21.sketch_text.stroke-4"),sQuery(id+"F0.wireOp",EDGE,"E21.sketch_text.stroke-5"),sQuery(id+"F0.wireOp",EDGE,"E21.sketch_text.stroke-6"),sQuery(id+"F0.wireOp",EDGE,"E21.sketch_text.stroke-7"),sQuery(id+"F0.wireOp",EDGE,"E21.sketch_text.stroke-8"),sQuery(id+"F0.wireOp",EDGE,"E21.sketch_text.stroke-9"),sQuery(id+"F0.wireOp",EDGE,"E21.sketch_text.stroke-10"),sQuery(id+"F0.wireOp",EDGE,"E21.sketch_text.stroke-11"),sQuery(id+"F0.wireOp",EDGE,"E21.sketch_text.stroke-12"),sQuery(id+"F0.wireOp",EDGE,"E21.sketch_text.stroke-13"),sQuery(id+"F0.wireOp",EDGE,"E21.sketch_text.stroke-14"),sQuery(id+"F0.wireOp",EDGE,"E21.sketch_text.stroke-15"),sQuery(id+"F0.wireOp",EDGE,"E21.sketch_text.stroke-16"),sQuery(id+"F0.wireOp",EDGE,"E21.sketch_text.stroke-17"),sQuery(id+"F0.wireOp",EDGE,"E21.sketch_text.stroke-18"),sQuery(id+"F0.wireOp",EDGE,"E22.sketch_text.stroke-0"),sQuery(id+"F0.wireOp",EDGE,"E22.sketch_text.stroke-1"),sQuery(id+"F0.wireOp",EDGE,"E22.sketch_text.stroke-2"),sQuery(id+"F0.wireOp",EDGE,"E22.sketch_text.stroke-3"),sQuery(id+"F0.wireOp",EDGE,"E22.sketch_text.stroke-4"),sQuery(id+"F0.wireOp",EDGE,"E22.sketch_text.stroke-5"),sQuery(id+"F0.wireOp",EDGE,"E22.sketch_text.stroke-6"),sQuery(id+"F0.wireOp",EDGE,"E22.sketch_text.stroke-7"),sQuery(id+"F0.wireOp",EDGE,"E22.sketch_text.stroke-8"),sQuery(id+"F0.wireOp",EDGE,"E22.sketch_text.stroke-9"),sQuery(id+"F0.wireOp",EDGE,"E22.sketch_text.stroke-10"),sQuery(id+"F0.wireOp",EDGE,"E22.sketch_text.stroke-11"),sQuery(id+"F0.wireOp",EDGE,"E22.sketch_text.stroke-12"),sQuery(id+"F0.wireOp",EDGE,"E22.sketch_text.stroke-13"),sQuery(id+"F0.wireOp",EDGE,"E23.sketch_text.stroke-0"),sQuery(id+"F0.wireOp",EDGE,"E23.sketch_text.stroke-1"),sQuery(id+"F0.wireOp",EDGE,"E23.sketch_text.stroke-2"),sQuery(id+"F0.wireOp",EDGE,"E23.sketch_text.stroke-3"),sQuery(id+"F0.wireOp",EDGE,"E23.sketch_text.stroke-4"),sQuery(id+"F0.wireOp",EDGE,"E23.sketch_text.stroke-5"),sQuery(id+"F0.wireOp",EDGE,"E23.sketch_text.stroke-6"),sQuery(id+"F0.wireOp",EDGE,"E23.sketch_text.stroke-7"),sQuery(id+"F0.wireOp",EDGE,"E23.sketch_text.stroke-8"),sQuery(id+"F0.wireOp",EDGE,"E23.sketch_text.stroke-9"),sQuery(id+"F0.wireOp",EDGE,"E23.sketch_text.stroke-10"),sQuery(id+"F0.wireOp",EDGE,"E23.sketch_text.stroke-11"),sQuery(id+"F0.wireOp",EDGE,"E23.sketch_text.stroke-12"),sQuery(id+"F0.wireOp",EDGE,"E23.sketch_text.stroke-13"),sQuery(id+"F0.wireOp",EDGE,"E23.sketch_text.stroke-14"),sQuery(id+"F0.wireOp",EDGE,"E24.sketch_text.stroke-0"),sQuery(id+"F0.wireOp",EDGE,"E24.sketch_text.stroke-1"),sQuery(id+"F0.wireOp",EDGE,"E24.sketch_text.stroke-2"),sQuery(id+"F0.wireOp",EDGE,"E24.sketch_text.stroke-3"),sQuery(id+"F0.wireOp",EDGE,"E24.sketch_text.stroke-4"),sQuery(id+"F0.wireOp",EDGE,"E24.sketch_text.stroke-5"),sQuery(id+"F0.wireOp",EDGE,"E24.sketch_text.stroke-6"),sQuery(id+"F0.wireOp",EDGE,"E24.sketch_text.stroke-7"),sQuery(id+"F0.wireOp",EDGE,"E24.sketch_text.stroke-8"),sQuery(id+"F0.wireOp",EDGE,"E24.sketch_text.stroke-9"),sQuery(id+"F0.wireOp",EDGE,"E24.sketch_text.stroke-10"),sQuery(id+"F0.wireOp",EDGE,"E24.sketch_text.stroke-11"),sQuery(id+"F0.wireOp",EDGE,"E24.sketch_text.stroke-12"),sQuery(id+"F0.wireOp",EDGE,"E24.sketch_text.stroke-13"),sQuery(id+"F0.wireOp",EDGE,"E24.sketch_text.stroke-14"),sQuery(id+"F0.wireOp",EDGE,"E24.sketch_text.stroke-15"),sQuery(id+"F0.wireOp",EDGE,"E24.sketch_text.stroke-16"),sQuery(id+"F0.wireOp",EDGE,"E24.sketch_text.stroke-17"),sQuery(id+"F0.wireOp",EDGE,"E25"),sQuery(id+"F0.wireOp",EDGE,"E26"),subQ1,subQ0])],"isStart":false})]});}
            var Q2;
            Q2=makeQuery(id+"F1.opExtrude","CAP_EDGE",EDGE,{"disambiguationData":[OSD([sQuery(id+"F0.wireOp",EDGE,"E28")])],"isStart":true});
            fillet(context, id + "F3", {"entities" : qUnion([Q0, Q1, Q2]), "radius" : 5.08 * mm, "tangentPropagation" : true, "allowEdgeOverflow" : false});
        }
    });
